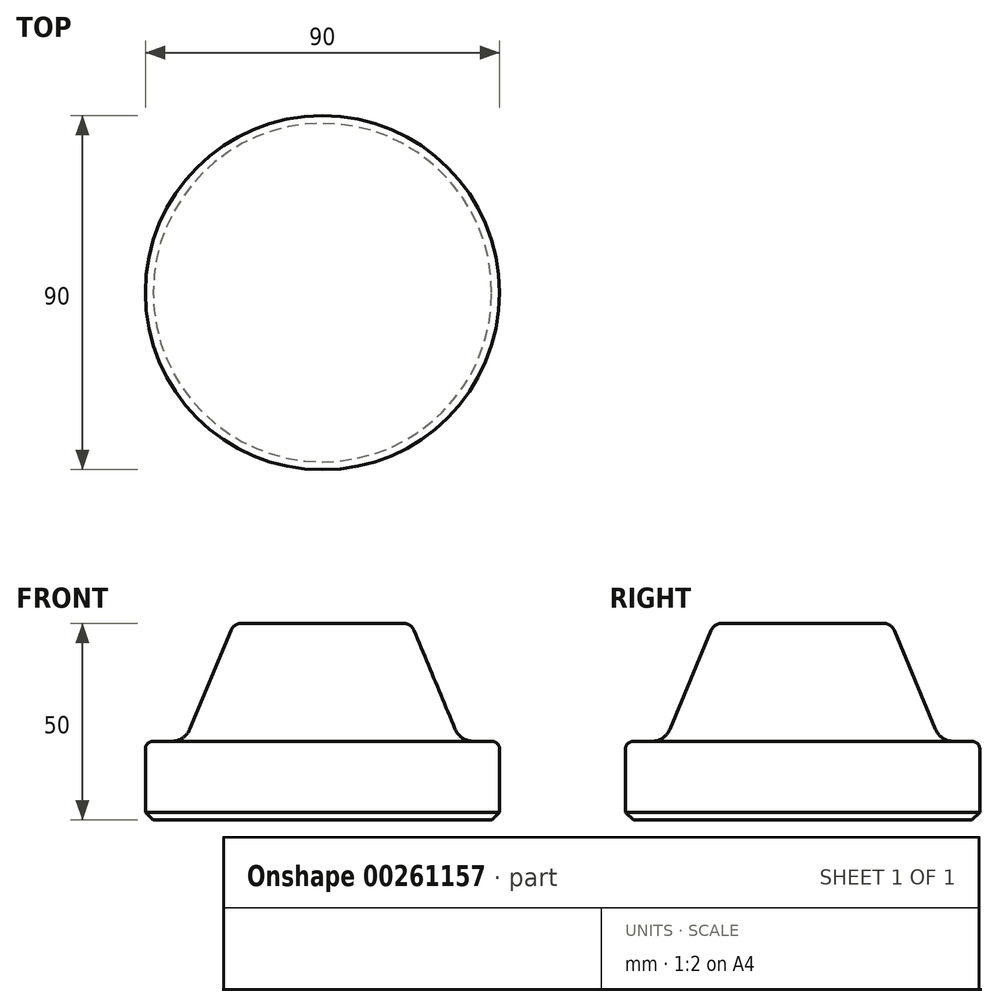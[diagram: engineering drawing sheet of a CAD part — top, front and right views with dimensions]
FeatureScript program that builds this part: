
annotation { "Feature Type Name" : "Feature", "Feature Type Description" : "" }
export const myFeature = defineFeature(function(context is Context, id is Id, definition is map)
    precondition{}
    {
        {
            var Q0;
            Q0=qCreatedBy(makeId("Front.planeOp"),FACE);
            var sketch = newSketch(context, id + "F0", { "sketchPlane" : qUnion([Q0])});
            skLineSegment(sketch, "E0", {"start": v(0, 50) * mm, "end": v(0, 0) * mm});
            skLineSegment(sketch, "E1", {"start": v(0, 0) * mm, "end": v(45, 0) * mm});
            skLineSegment(sketch, "E2", {"start": v(45, 0) * mm, "end": v(45, 18) * mm});
            skLineSegment(sketch, "E3", {"start": v(43, 20) * mm, "end": v(38.33, 20) * mm});
            skLineSegment(sketch, "E4", {"start": v(0, 50) * mm, "end": v(20.5, 50) * mm});
            skLineSegment(sketch, "E5", {"start": v(23.27, 48.15) * mm, "end": v(33.72, 23.08) * mm});
            skPoint(sketch, "E6.visualSharp", {"position": v(22.5, 50) * mm});
            skArc(sketch, "E6.filletArc", {"start": v(23.27, 48.15) * mm, "mid": v(22.16, 49.5) * mm, "end": v(20.5, 50) * mm});
            skPoint(sketch, "E7.visualSharp", {"position": v(35, 20) * mm});
            skArc(sketch, "E7.filletArc", {"start": v(33.72, 23.08) * mm, "mid": v(35.56, 20.84) * mm, "end": v(38.33, 20) * mm});
            skPoint(sketch, "E8.visualSharp", {"position": v(45, 20) * mm});
            skArc(sketch, "E8.filletArc", {"start": v(45, 18) * mm, "mid": v(44.41, 19.41) * mm, "end": v(43, 20) * mm});
            skLineSegment(sketch, "E9", {"start": v(0, 68.65) * mm, "end": v(0, -23.98) * mm, "construction": true});
            skPoint(sketch, "E9.endSnap0", {"position": v(0, 25) * mm});
            skSolve(sketch);
        }
        {
            var Q0;
            Q0=makeQuery(id+"F0.imprint","IMPRINT",FACE,{"disambiguationData":[TD([[makeQuery(id+"F0.imprint","IMPRINT",EDGE,{"derivedFrom":sQuery(id+"F0.wireOp",EDGE,"E0")}),1.0]])]});
            var Q1;
            Q1=sQuery(id+"F0.wireOp",EDGE,"E9");
            revolve(context, id + "F1", {"entities" : qUnion([Q0]), "axis" : qUnion([Q1]), "revolveType" : RevolveType.FULL});
        }
        {
            var Q0;
            Q0=makeQuery(id+"F1.opRevolve","SWEPT_EDGE",EDGE,{"disambiguationData":[OSD([sQuery(id+"F0.wireOp",EDGE,"E1"),sQuery(id+"F0.wireOp",EDGE,"E2")])]});
            chamfer(context, id + "F2", {"entities" : qUnion([Q0]), "width" : 2 * mm, "tangentPropagation" : true});
        }
    });
